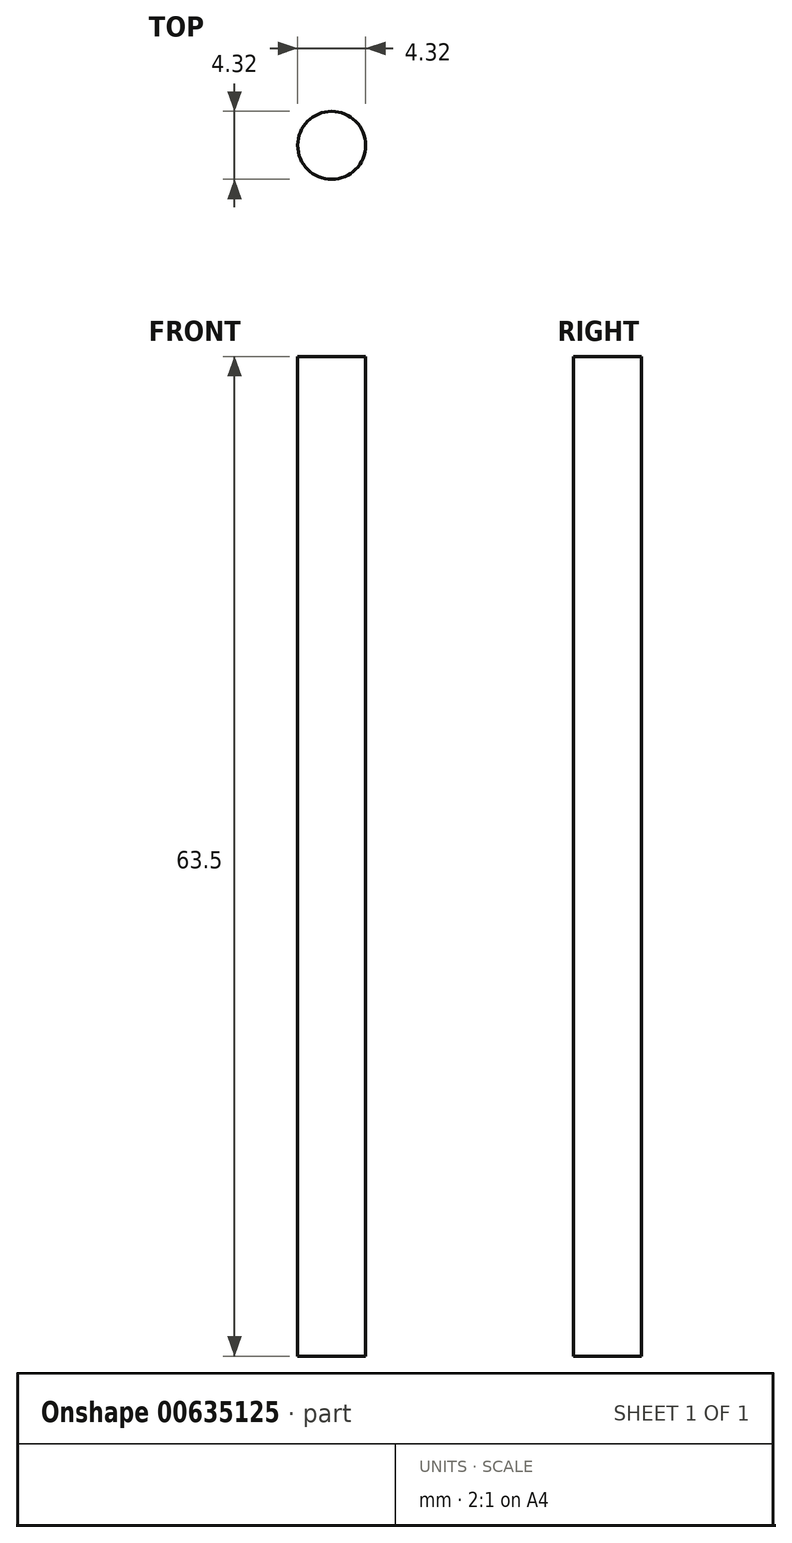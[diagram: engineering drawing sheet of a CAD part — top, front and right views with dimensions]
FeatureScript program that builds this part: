
annotation { "Feature Type Name" : "Feature", "Feature Type Description" : "" }
export const myFeature = defineFeature(function(context is Context, id is Id, definition is map)
    precondition{}
    {
        {
            var Q0;
            Q0=qCreatedBy(makeId("Top.planeOp"),FACE);
            var sketch = newSketch(context, id + "F0", { "sketchPlane" : qUnion([Q0])});
            skCircle(sketch, "E0", {"center": v(0, 0) * mm, "radius": 2.16 * mm});
            skSolve(sketch);
        }
        {
            var Q0;
            Q0=makeQuery(id+"F0.imprint","IMPRINT",FACE,{"disambiguationData":[TD([[makeQuery(id+"F0.imprint","IMPRINT",EDGE,{"derivedFrom":sQuery(id+"F0.wireOp",EDGE,"E0")}),1.0]])]});
            extrude(context, id + "F1", {"entities" : qUnion([Q0]), "depth" : 63.5 * mm, "offsetDistance" : 25.4 * mm});
        }
    });
